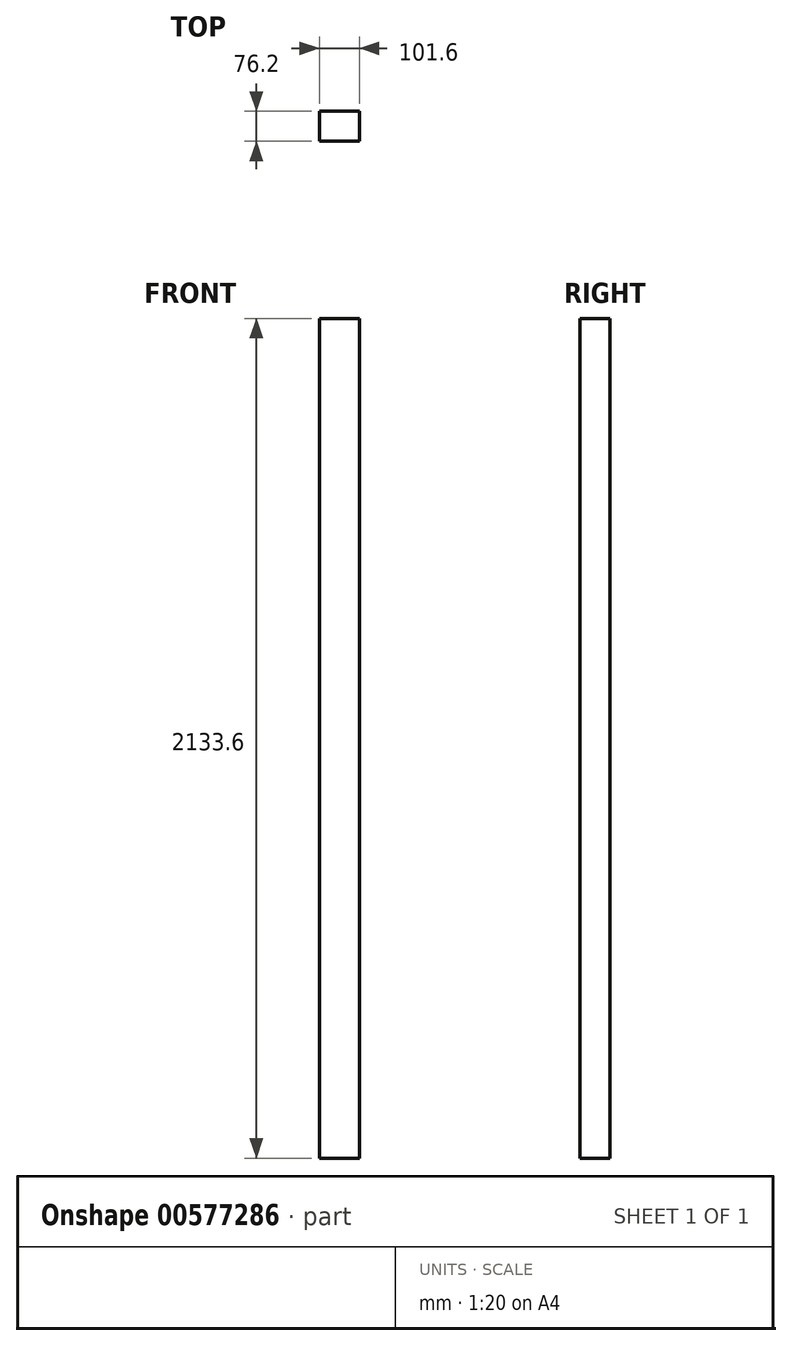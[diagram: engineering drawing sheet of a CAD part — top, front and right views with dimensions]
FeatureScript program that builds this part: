
annotation { "Feature Type Name" : "Feature", "Feature Type Description" : "" }
export const myFeature = defineFeature(function(context is Context, id is Id, definition is map)
    precondition{}
    {
        {
            var Q0;
            Q0=qCreatedBy(makeId("Front.planeOp"),FACE);
            var sketch = newSketch(context, id + "F0", { "sketchPlane" : qUnion([Q0])});
            skLineSegment(sketch, "E0.bottom", {"start": v(0, 0) * mm, "end": v(101.6, 0) * mm});
            skLineSegment(sketch, "E0.top", {"start": v(0, 2133.6) * mm, "end": v(101.6, 2133.6) * mm});
            skLineSegment(sketch, "E0.left", {"start": v(0, 0) * mm, "end": v(0, 2133.6) * mm});
            skLineSegment(sketch, "E0.right", {"start": v(101.6, 0) * mm, "end": v(101.6, 2133.6) * mm});
            skSolve(sketch);
        }
        {
            var Q0;
            Q0=makeQuery(id+"F0.imprint","IMPRINT",FACE,{"disambiguationData":[TD([[makeQuery(id+"F0.imprint","IMPRINT",EDGE,{"derivedFrom":sQuery(id+"F0.wireOp",EDGE,"E0.bottom")}),1.0]])]});
            extrude(context, id + "F1", {"entities" : qUnion([Q0]), "depth" : 76.2 * mm, "offsetDistance" : 25.4 * mm});
        }
    });
